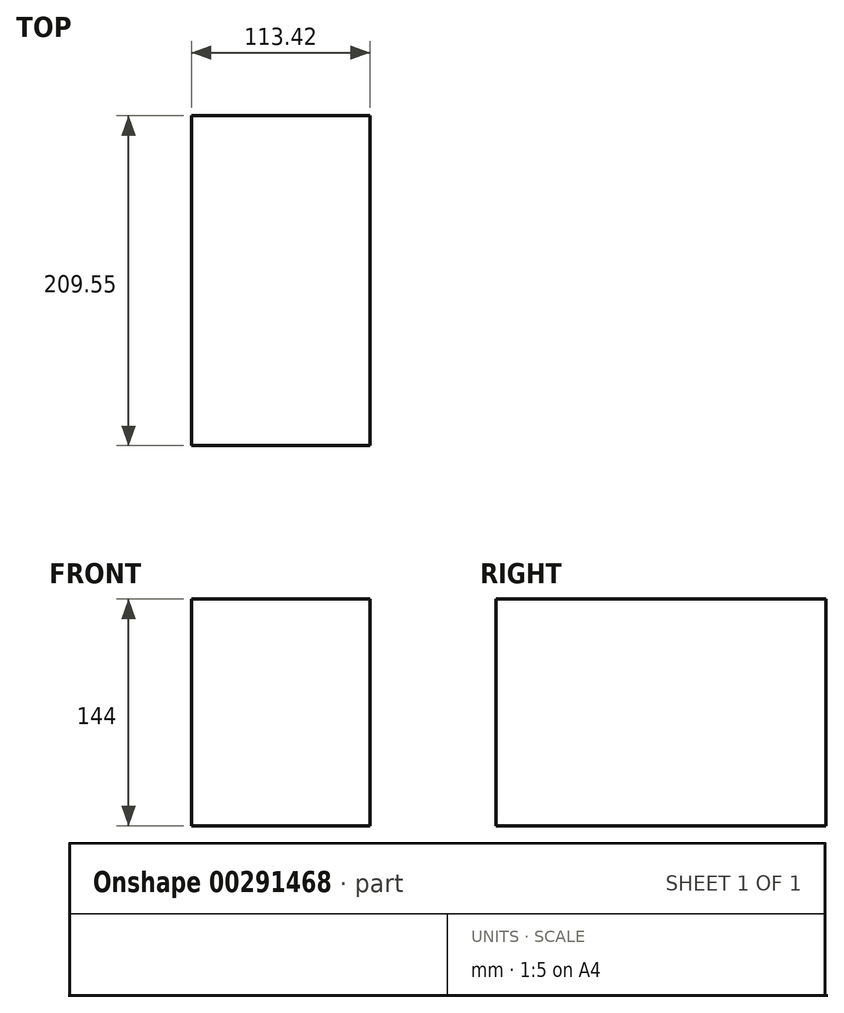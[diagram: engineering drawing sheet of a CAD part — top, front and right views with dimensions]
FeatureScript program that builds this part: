
annotation { "Feature Type Name" : "Feature", "Feature Type Description" : "" }
export const myFeature = defineFeature(function(context is Context, id is Id, definition is map)
    precondition{}
    {
        {
            var Q0;
            Q0=qCreatedBy(makeId("Front.planeOp"),FACE);
            var sketch = newSketch(context, id + "F0", { "sketchPlane" : qUnion([Q0])});
            skLineSegment(sketch, "E0.bottom", {"start": v(0, 0) * mm, "end": v(113.42, 0) * mm});
            skLineSegment(sketch, "E0.top", {"start": v(0, 144) * mm, "end": v(113.42, 144) * mm});
            skLineSegment(sketch, "E0.left", {"start": v(0, 0) * mm, "end": v(0, 144) * mm});
            skLineSegment(sketch, "E0.right", {"start": v(113.42, 0) * mm, "end": v(113.42, 144) * mm});
            skLineSegment(sketch, "E1.bottom", {"start": v(48.99, 177.8) * mm, "end": v(0, 177.8) * mm, "construction": true});
            skLineSegment(sketch, "E1.top", {"start": v(48.99, 160.64) * mm, "end": v(0, 160.64) * mm, "construction": true});
            skLineSegment(sketch, "E1.left", {"start": v(48.99, 177.8) * mm, "end": v(48.99, 160.64) * mm, "construction": true});
            skLineSegment(sketch, "E1.right", {"start": v(0, 177.8) * mm, "end": v(0, 160.64) * mm, "construction": true});
            skLineSegment(sketch, "E2.bottom", {"start": v(106.12, 188.88) * mm, "end": v(82.6, 188.88) * mm, "construction": true});
            skLineSegment(sketch, "E2.top", {"start": v(106.12, 113.99) * mm, "end": v(82.6, 113.99) * mm, "construction": true});
            skLineSegment(sketch, "E2.left", {"start": v(106.12, 188.88) * mm, "end": v(106.12, 113.99) * mm, "construction": true});
            skLineSegment(sketch, "E2.right", {"start": v(82.6, 188.88) * mm, "end": v(82.6, 113.99) * mm, "construction": true});
            skSolve(sketch);
        }
        {
            var Q0;
            Q0 = qSketchRegion(id + "F0", true);
            extrude(context, id + "F1", {"entities" : qUnion([Q0]), "depth" : 209.55 * mm});
        }
    });
